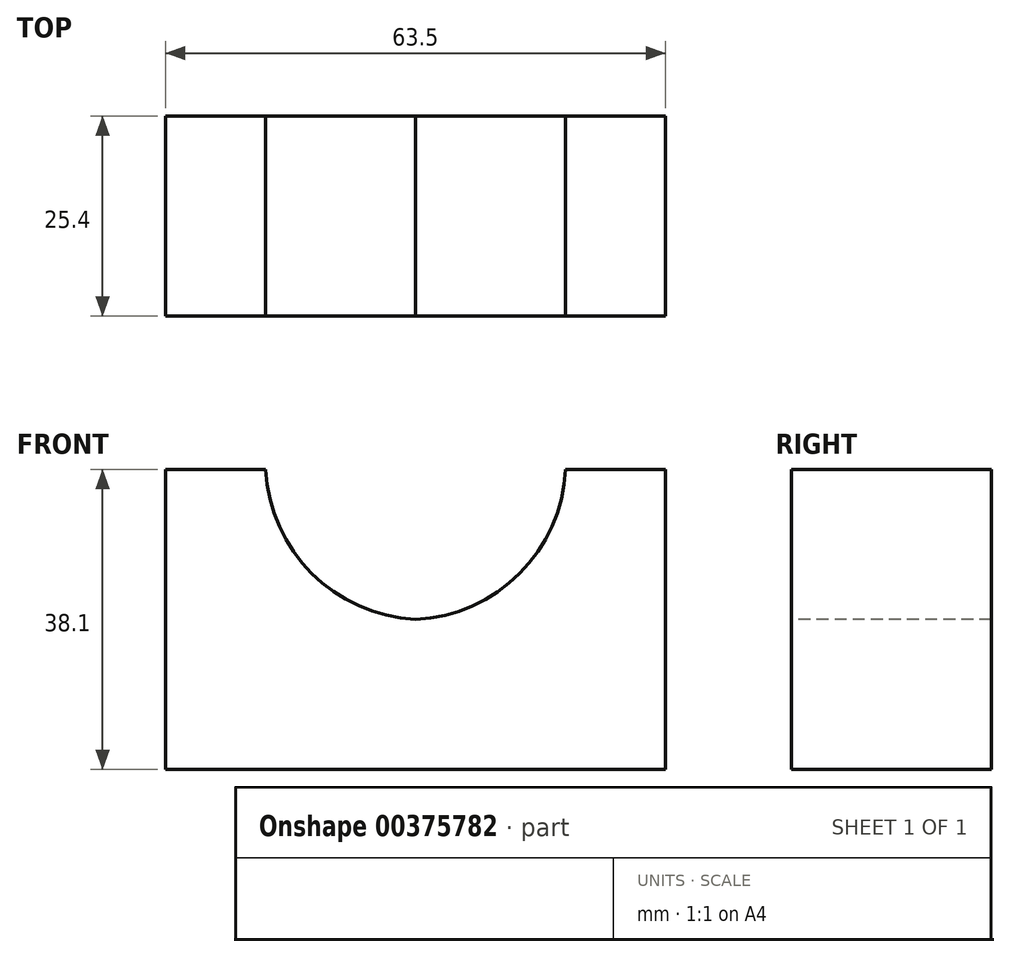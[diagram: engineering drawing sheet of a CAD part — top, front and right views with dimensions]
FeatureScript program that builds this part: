
annotation { "Feature Type Name" : "Feature", "Feature Type Description" : "" }
export const myFeature = defineFeature(function(context is Context, id is Id, definition is map)
    precondition{}
    {
        {
            var Q0;
            Q0=qCreatedBy(makeId("Front.planeOp"),FACE);
            var sketch = newSketch(context, id + "F0", { "sketchPlane" : qUnion([Q0])});
            skLineSegment(sketch, "E0", {"start": v(-63.5, 0) * mm, "end": v(-63.5, 38.1) * mm});
            skLineSegment(sketch, "E1", {"start": v(-63.5, 38.1) * mm, "end": v(0, 38.1) * mm});
            skLineSegment(sketch, "E2", {"start": v(0, 38.1) * mm, "end": v(0, 0) * mm});
            skLineSegment(sketch, "E3", {"start": v(0, 0) * mm, "end": v(-63.5, 0) * mm});
            skSolve(sketch);
        }
        {
            var Q0;
            Q0=makeQuery(id+"F0.imprint","IMPRINT",FACE,{"disambiguationData":[TD([[makeQuery(id+"F0.imprint","IMPRINT",EDGE,{"derivedFrom":sQuery(id+"F0.wireOp",EDGE,"E0")}),-1.0]])]});
            extrude(context, id + "F1", {"entities" : qUnion([Q0]), "depth" : 25.4 * mm});
        }
        {
            var Q0;
            Q0=makeQuery(id+"F1.opExtrude","CAP_FACE",FACE,{"disambiguationData":[OSD([sQuery(id+"F0.wireOp",EDGE,"E0"),sQuery(id+"F0.wireOp",EDGE,"E1"),sQuery(id+"F0.wireOp",EDGE,"E2"),sQuery(id+"F0.wireOp",EDGE,"E3")])],"isStart":false});
            var sketch = newSketch(context, id + "F2", { "sketchPlane" : qUnion([Q0])});
            skArc(sketch, "E4", {"start": v(-31.75, 19.05) * mm, "mid": v(-18.53, 24.88) * mm, "end": v(-12.7, 38.1) * mm});
            skPoint(sketch, "E4.startSnap0", {"position": v(-31.75, 38.1) * mm});
            skArc(sketch, "E5", {"start": v(-50.8, 38.1) * mm, "mid": v(-44.93, 24.92) * mm, "end": v(-31.75, 19.05) * mm});
            skLineSegment(sketch, "E6", {"start": v(-50.8, 38.1) * mm, "end": v(-31.75, 38.1) * mm});
            skSolve(sketch);
        }
        {
            var Q0;
            {var subQ0=sQuery(id+"F2.wireOp",EDGE,"E4");Q0=makeQuery(id+"F2.imprint","IMPRINT",FACE,{"disambiguationData":[TD([[makeQuery(id+"F2.imprint","IMPRINT",EDGE,{"derivedFrom":subQ0}),1.0]])]});}
            extrude(context, id + "F3", {"entities" : qUnion([Q0]), "operationType" : NewBodyOperationType.REMOVE, "oppositeDirection" : true, "depth" : 25.4 * mm});
        }
    });
